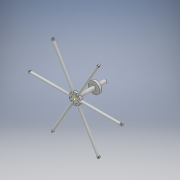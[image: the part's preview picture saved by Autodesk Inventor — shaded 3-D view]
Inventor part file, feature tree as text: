
AUTODESK INVENTOR PART (.ipt)
format: ipt  version: 2018 (Build 220112000, 112)  size: 234,496 bytes
history: native  units: mm
features: sketch x8, extrude x7, pattern_circular x6, plane x2, mirror x1, projected_geometry x1
ambient origin geometry x8: Origin, YZ Plane, XZ Plane, XY Plane, X Axis, Y Axis, Z Axis, Center Point
bodies: Solid1 (feature_tree)
feature tree (25):
  extrude  "Extrusion3"  Depth=30.0mm
  plane  "Work Plane2"
  mirror  "Mirror1"
  plane  "Work Plane5"
  extrude  "Extrusion4"  Depth=75.0mm
  pattern_circular  "Circular Pattern2"  Count=40  [1 undecoded]
  extrude  "Extrusion5"  Depth=10.0mm
  pattern_circular  "Circular Pattern3"  Count=25  [1 undecoded]
  pattern_circular  "Circular Pattern4"  Count=6 Angle=360.0deg
  sketch  "Sketch7"  dims[d35=30.0mm d36=10.0mm d37=50.0mm d38=0.0mm]
  extrude  "Extrusion6"  Depth=10.0mm TaperAngle=360.0deg
  pattern_circular  "Circular Pattern5"  Count=6 Angle=360.0deg
  extrude  "Extrusion7"  Depth=10.0mm
  pattern_circular  "Circular Pattern6"  Count=5  [1 undecoded]
  sketch  "Sketch3"  dims[d13=250.0mm d14=0.0mm d16=75.0mm d19=400.0mm]
  sketch  "Sketch5"  dims[d20=20.0mm d21=10.0mm d22=250.0mm d23=0.0mm d24=60.0mm d25=360.0deg]
  projected_geometry  "Projected Loop1"
  sketch  "Sketch6"  dims[d27=10.0mm d28=0.0mm d29=60.0mm d30=360.0deg d32=60.0mm d33=360.0deg]
  sketch  "Sketch8"  dims[d39=60.0mm d40=360.0deg d42=10.0mm d43=50.0mm d44=0.0mm]
  sketch  "Sketch9"  dims[d45=60.0mm d46=360.0deg]
  sketch  "Sketch1"  dims[d0=100.0mm d2=0.0mm d3=20.0mm]
  sketch  "Sketch2"  dims[d4=21.0mm d6=0.0mm d7=20.0mm d8=360.0deg d10=60.0mm d12=30.0mm]
  extrude  "Extrusion1"  Depth=10.0mm
  pattern_circular  "Circular Pattern1"  Count=5  [1 undecoded]
  extrude  "Extrusion2"  [1 undecoded]
note: 5 required parameter values undecoded (feature->parameter linkage not recoverable at this tier; creation-order binding heuristic only, values carry confidence <= 0.55)
